FCSTD DOCUMENT  (FreeCAD 0.21R33675 (Git))
Label: Tail_Hinge_Junction
License: All rights reserved
LicenseURL: http://en.wikipedia.org/wiki/All_rights_reserved
objects: App::Link×3, Spreadsheet::Sheet×1, App::Part×1
EXTERNAL_REF file=../../../Master_of_Puppets.FCStd obj=Spreadsheet
EXTERNAL_REF file=../../../Master_of_Puppets.FCStd obj=Tail
EXTERNAL_REF file=Tail_Hinge_Junction_Cover_Top.FCStd obj=PocketBody
EXTERNAL_REF file=Tail_Hinge_Junction_Cover_Side.FCStd obj=PadBody

FEATURE [Spreadsheet::Sheet] Spreadsheet
  cells = A1='Inputs; A2='YawPipeDiameter; B2(YawPipeDiameter)==Master_of_Puppets#Spreadsheet.YawPipeDiameter; A3='HingeInnerPipeRadius; B3(HingeInnerPipeRadius)==Master_of_Puppets#Tail.HingeInnerPipeRadius; A4='FlatMetalThickness; B4(FlatMetalThickness)==Master_of_Puppets#Spreadsheet.FlatMetalThickness; A5='Height; B5(Height)==Master_of_Puppets#Tail.TailHingeJunctionHeight; A6='FullWidth; B6(FullWidth)==Master_of_Puppets#Tail.TailHingeJunctionFullWidth; A7='Calculated; A8='YawPipeRadius; B8(YawPipeRadius)==YawPipeDiameter / 2; A9='SideCoverAngle; B9(SideCoverAngle)==YawPipeRadius == HingeInnerPipeRadius ? 0 deg : 90 deg - atan(FullWidth / (YawPipeRadius - HingeInnerPipeRadius)); A10='TailHingeTopCoverZ; B10(TailHingeTopCoverZ)==Height - FlatMetalThickness; A11='FrontTailHingeSideCoverY; B11(FrontTailHingeSideCoverY)==-YawPipeRadius; A12='BackTailHingeSideCoverY; B12(BackTailHingeSideCoverY)==YawPipeRadius + FlatMetalThickness
FEATURE [App::Link] Link  label="Top_Cover"
  LinkPlacement = pos=(0,0,70) rot=(0,0,1;0rad)
  LinkedObject = -> <external Tail_Hinge_Junction_Cover_Top.FCStd>#PocketBody
  Placement = pos=(0,0,70) rot=(0,0,1;0rad)
  expr: .Placement.Base.z = Spreadsheet.TailHingeTopCoverZ
FEATURE [App::Link] Link001  label="Cover_Side_Front"
  LinkPlacement = pos=(0,-30.15,0) rot=(0,0,1;0rad)
  LinkTransform = true
  LinkedObject = -> <external Tail_Hinge_Junction_Cover_Side.FCStd>#PadBody
  Placement = pos=(0,-30.15,0) rot=(0,0,1;0rad)
  expr: .LinkPlacement.Base.y = Spreadsheet.FrontTailHingeSideCoverY
  expr: .LinkPlacement.Rotation.Angle = Spreadsheet.SideCoverAngle
FEATURE [App::Link] Link002  label="Cover_Side_Back"
  LinkPlacement = pos=(0,40.15,0) rot=(0,0,1;0rad)
  LinkTransform = true
  LinkedObject = -> <external Tail_Hinge_Junction_Cover_Side.FCStd>#PadBody
  Placement = pos=(0,40.15,0) rot=(0,0,1;0rad)
  expr: .LinkPlacement.Base.y = Spreadsheet.BackTailHingeSideCoverY
  expr: .LinkPlacement.Rotation.Angle = -Spreadsheet.SideCoverAngle
FEATURE [App::Part] Part  label="Tail_Hinge_Junction"
  Group = -> [Link,Link001,Link002]
  Origin = -> Origin

RESOLVED EXTERNAL PARTS (link-assembly join: the EXTERNAL_REF files above that resolve inside this repo's crawl, each included once):
---- part ../../../Master_of_Puppets.FCStd = doc fcstd_6404554055c4 (61625 chars; too large to inline — full recipe in that document) ----
---- part Tail_Hinge_Junction_Cover_Side.FCStd = doc fcstd_45b42fe11e72 ----
FCSTD DOCUMENT  (FreeCAD 0.19R24366 (Git))
Label: Tail_Hinge_Junction_Cover_Side
License: All rights reserved
LicenseURL: http://en.wikipedia.org/wiki/All_rights_reserved
objects: Sketcher::SketchObject×1, PartDesign::Pad×1, Spreadsheet::Sheet×1, PartDesign::Body×1
note: 4 computed .brp shape members not serialized (recipe doc carries the construction recipe); baked Part::Feature solids carry a one-line shape summary decoded from their .brp
EXTERNAL_REF file=../../../Master_of_Puppets.FCStd obj=Spreadsheet
EXTERNAL_REF file=../../../Master_of_Puppets.FCStd obj=Tail

FEATURE [Sketcher::SketchObject] Sketch
  FullyConstrained = true
  MapMode = 5
  Support = -> [XY_Plane001]
  expr: Constraints[18] = Spreadsheet.VerticalPlaneAngle
  expr: Constraints[16] = Spreadsheet.Width
  expr: Constraints[17] = Spreadsheet.TailHingeJunctionFullWidth
  expr: Constraints[14] = Spreadsheet.Height
  expr: Constraints[15] = Spreadsheet.Width
  sketch-geometry (7):
    g0: LineSegment StartX=0 StartY=0 StartZ=0 EndX=54.3 EndY=0 EndZ=0
    g1: LineSegment StartX=54.3 StartY=0 StartZ=0 EndX=79.7779 EndY=70 EndZ=0
    g2: LineSegment StartX=79.7779 StartY=70 StartZ=0 EndX=54.3 EndY=80 EndZ=0
    g3: LineSegment StartX=54.3 StartY=80 StartZ=0 EndX=0 EndY=80 EndZ=0
    g4: LineSegment StartX=0 StartY=80 StartZ=0 EndX=0 EndY=0 EndZ=0
    g5: LineSegment StartX=54.3 StartY=80 StartZ=0 EndX=83.4176 EndY=80 EndZ=0
    g6: LineSegment StartX=83.4176 StartY=80 StartZ=0 EndX=79.7779 EndY=70 EndZ=0
  constraints (19):
    c: Coincident(g-1,g0)
    c: PointOnObject(g0,g-1)
    c: Coincident(g0,g1)
    c: Coincident(g1,g2)
    c: Coincident(g2,g3)
    c: Horizontal(g3)
    c: Coincident(g3,g4)
    c: Vertical(g4)
    c: Coincident(g4,g-1)
    c: Coincident(g2,g5)
    c: Horizontal(g5)
    c: Coincident(g5,g6)
    c: Coincident(g6,g1)
    c: Parallel(g6,g1)
    c: Distance(g4) = 80
    c: DistanceX(g0,g0) = 54.3
    c: Distance(g3) = 54.3
    c: Distance(g1,g4) = 79.7779
    c: Angle(g1,g4) = 0.349066
FEATURE [PartDesign::Pad] Pad
  AllowMultiFace = false
  Direction = (1,1,1)
  Length = 10
  Length2 = 100
  Profile = -> Sketch
  Type = 0
  expr: Length = Spreadsheet.FlatMetalThickness
FEATURE [Spreadsheet::Sheet] Spreadsheet
  cells = A1=Inputs; A2=YawPipeDiameter; B2(YawPipeDiameter)==Master_of_Puppets#Spreadsheet.YawPipeDiameter; A3=HingeInnerPipeRadius; B3(HingeInnerPipeRadius)==Master_of_Puppets#Tail.HingeInnerPipeRadius; A4=VerticalPlaneAngle; B4(VerticalPlaneAngle)==Master_of_Puppets#Spreadsheet.VerticalPlaneAngle; A5=FlatMetalThickness; B5(FlatMetalThickness)==Master_of_Puppets#Spreadsheet.FlatMetalThickness; A6=Height; B6(Height)==Master_of_Puppets#Tail.TailHingeJunctionHeight; A7=TailHingeJunctionFullWidth; B7(TailHingeJunctionFullWidth)==Master_of_Puppets#Tail.TailHingeJunctionFullWidth; A8=Calculated; A9=YawPipeRadius; B9(YawPipeRadius)==YawPipeDiameter / 2; A10=Width; B10(Width)==YawPipeRadius + HingeInnerPipeRadius
FEATURE [PartDesign::Body] PadBody  label="Tail_Hinge_Junction_Cover_Side"
  Group = -> [Sketch,Pad]
  Openafpm_Flat = true
  Origin = -> Origin001
  Placement = pos=(0,0,0) rot=(1,0,0;1.5708rad)
  Tip = -> Pad
---- part Tail_Hinge_Junction_Cover_Top.FCStd = doc fcstd_133b7b8cf6cf ----
FCSTD DOCUMENT  (FreeCAD 1.0R39109 (Git))
Label: Tail_Hinge_Junction_Cover_Top
License: All rights reserved
LicenseURL: http://en.wikipedia.org/wiki/All_rights_reserved
objects: Sketcher::SketchObject×1, PartDesign::Pad×1, Spreadsheet::Sheet×1, PartDesign::Body×1, TechDraw::DrawSVGTemplate×1, TechDraw::DrawProjGroupItem×1, TechDraw::DrawViewDimension×1, TechDraw::DrawPage×1
note: 8 computed .brp shape members not serialized (recipe doc carries the construction recipe); baked Part::Feature solids carry a one-line shape summary decoded from their .brp
EXTERNAL_REF file=../../../Master_of_Puppets.FCStd obj=Spreadsheet
EXTERNAL_REF file=../../../Master_of_Puppets.FCStd obj=Tail

FEATURE [Sketcher::SketchObject] Sketch
  ArcFitTolerance = 0
  AttachmentSupport = -> [XY_Plane001]
  FullyConstrained = true
  MakeInternals = false
  MapMode = 5
  expr: Constraints[14] = Spreadsheet.Chamfer
  expr: Constraints[16] = Spreadsheet.YawPipeRadius
  expr: Constraints[1] = Spreadsheet.HingeInnerPipeRadius
  expr: Constraints[22] = Spreadsheet.Chamfer
  expr: Constraints[2] = Spreadsheet.FullWidth
  sketch-geometry (14):
    g0: ArcOfCircle [constr] CenterX=79.7779 CenterY=0 CenterZ=0 NormalX=0 NormalY=0 NormalZ=1 AngleXU=0 Radius=24.15 StartAngle=1.49656 EndAngle=4.78663
    g1: Circle [constr] CenterX=0 CenterY=0 CenterZ=0 NormalX=0 NormalY=0 NormalZ=1 AngleXU=0 Radius=30.15
    g2: ArcOfCircle CenterX=0 CenterY=0 CenterZ=0 NormalX=0 NormalY=0 NormalZ=1 AngleXU=0 Radius=30.15 StartAngle=5.23599 EndAngle=7.33038
    g3: LineSegment StartX=15.075 StartY=-26.1107 StartZ=0 EndX=15.075 EndY=-29.0288 EndZ=0
    g4: ArcOfCircle CenterX=79.7779 CenterY=0 CenterZ=0 NormalX=0 NormalY=0 NormalZ=1 AngleXU=0 Radius=24.15 StartAngle=2.15323 EndAngle=4.12996
    g5: LineSegment StartX=66.4941 StartY=-20.1683 StartZ=0 EndX=66.4941 EndY=-25.2047 EndZ=0
    g6: LineSegment [constr] StartX=0 StartY=30.15 StartZ=0 EndX=15.075 EndY=30.15 EndZ=0
    g7: LineSegment [constr] StartX=0 StartY=30.15 StartZ=0 EndX=81.5691 EndY=24.0835 EndZ=0
    g8: LineSegment [constr] StartX=81.5691 StartY=24.0835 StartZ=0 EndX=66.4941 EndY=24.0835 EndZ=0
    g9: LineSegment StartX=15.075 StartY=-29.0288 StartZ=0 EndX=66.4941 EndY=-25.2047 EndZ=0
    g10: LineSegment [constr] StartX=81.5691 StartY=-24.0835 StartZ=0 EndX=0 EndY=-30.15 EndZ=0
    g11: LineSegment StartX=66.4941 StartY=25.2047 StartZ=0 EndX=15.075 EndY=29.0288 EndZ=0
    g12: LineSegment StartX=15.075 StartY=29.0288 StartZ=0 EndX=15.075 EndY=26.1107 EndZ=0
    g13: LineSegment StartX=66.4941 StartY=25.2047 StartZ=0 EndX=66.4941 EndY=20.1683 EndZ=0
  constraints (44):
    c: PointOnObject(g0,g-1)
    c: Radius(g0) = 24.15
    c: DistanceX(g-1,g0) = 79.7779
    c: Coincident(g1,g-1)
    c: Coincident(g2,g1)
    c: PointOnObject(g2,g1)
    c: Vertical(g2,g2)
    c: Coincident(g3,g2)
    c: Vertical(g3)
    c: Coincident(g4,g0)
    c: Coincident(g5,g4)
    c: Vertical(g4,g4)
    c: Vertical(g4,g5)
    c: PointOnObject(g4,g0)
    c: Distance(g6) = 15.075
    c: Vertical(g9,g6)
    c: Radius(g1) = 30.15
    c: PointOnObject(g7,g1)
    c: Coincident(g7,g0)
    c: PointOnObject(g7,g-2)
    c: Coincident(g8,g7)
    c: Horizontal(g8)
    c: Distance(g8) = 15.075
    c: Coincident(g10,g0)
    c: PointOnObject(g10,g-2)
    c: PointOnObject(g10,g1)
    c: Perpendicular(g-2,g6)
    c: Coincident(g6,g7)
    c: Tangent(g10,g0,g0) = 1.5708
    c: Tangent(g0,g7,g7) = 1.5708
    c: PointOnObject(g9,g10)
    c: PointOnObject(g3,g10)
    c: PointOnObject(g9,g10)
    c: PointOnObject(g11,g7)
    c: PointOnObject(g11,g7)
    c: Coincident(g12,g11)
    c: Coincident(g12,g2)
    c: Coincident(g5,g9)
    c: Vertical(g8,g11)
    c: Vertical(g11,g6)
    c: Vertical(g2,g11)
    c: Coincident(g13,g11)
    c: Coincident(g13,g4)
    c: Vertical(g13)
FEATURE [PartDesign::Pad] Pad
  AllowMultiFace = false
  Direction = (0,0,1)
  Length = 10
  Length2 = 100
  Profile = -> Sketch
  Suppressed = false
  Type = 0
  expr: Length = Spreadsheet.FlatMetalThickness
FEATURE [Spreadsheet::Sheet] Spreadsheet
  cells = A1='Inputs; A2='YawPipeDiameter; B2(YawPipeDiameter)==Master_of_Puppets#Spreadsheet.YawPipeDiameter; A3='HingeInnerPipeRadius; B3(HingeInnerPipeRadius)==Master_of_Puppets#Tail.HingeInnerPipeRadius; A4='FlatMetalThickness; B4(FlatMetalThickness)==Master_of_Puppets#Spreadsheet.FlatMetalThickness; A5='FullWidth; B5(FullWidth)==Master_of_Puppets#Tail.TailHingeJunctionFullWidth; A6='Chamfer; B6(Chamfer)==Master_of_Puppets#Tail.TailHingeJunctionChamfer; A7='Calculated; A8='YawPipeRadius; B8(YawPipeRadius)==YawPipeDiameter / 2; A9='XOffset; B9(XOffset)==-Chamfer
FEATURE [PartDesign::Body] PocketBody  label="Tail_Hinge_Junction_Cover_Top"
  AllowCompound = false
  Group = -> [Sketch,Pad]
  Openafpm_Flat = true
  Origin = -> Origin001
  Tip = -> Pad
FEATURE [TechDraw::DrawSVGTemplate] Template
  Height = 210
  Orientation = 1
  Template = <userpath>/micromamba/envs/openafpm-cad-core/share/Mod/TechDraw/Templates/Default_Template_A4_Landscape.svg
  Width = 297
FEATURE [TechDraw::DrawProjGroupItem] View
  CoarseView = false
  Direction = (0,0,1)
  Focus = 100
  HardHidden = false
  IsoCount = 0
  IsoHidden = false
  IsoVisible = false
  LockPosition = false
  Perspective = false
  Rotation = 0
  RotationVector = (1,0,0)
  ScaleType = 0
  ScrubCount = 1
  SeamHidden = false
  SeamVisible = false
  SmoothHidden = false
  SmoothVisible = true
  Source = -> [PocketBody]
  Type = 0
  X = 148.5
  XDirection = (1,0,0)
  Y = 105
FEATURE [TechDraw::DrawViewDimension] Dimension  label="D"
  AngleOverride = false
  Arbitrary = true
  ArbitraryTolerances = false
  BoxCorners = (2) [(-25.7095,-29.0288,0),(25.7095,29.0288,0)]
  EqualTolerance = true
  ExtensionAngle = 0
  FormatSpec = D
  FormatSpecOverTolerance = %+.2w
  FormatSpecUnderTolerance = %+.2w
  Inverted = false
  LineAngle = 0
  LockPosition = false
  MeasureType = 1
  OverTolerance = 0
  References2D = -> [View]
  Rotation = 0
  ScaleType = 0
  TheoreticalExact = false
  Type = 0
  UnderTolerance = 0
  X = 2.10442
  Y = 4.19322
FEATURE [TechDraw::DrawPage] Page
  KeepUpdated = true
  NextBalloonIndex = 1
  ProjectionType = 0
  Template = -> Template
  Views = -> [View,Dimension]
